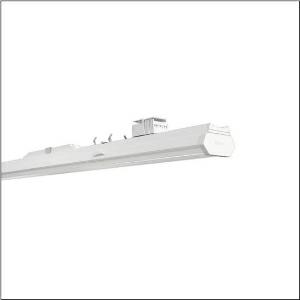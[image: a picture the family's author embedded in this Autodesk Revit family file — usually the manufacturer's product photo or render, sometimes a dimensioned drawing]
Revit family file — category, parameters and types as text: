
# Revit family: licross_r__11_protected_mo_51tp12dn495g3s4_346c
name_source: partatom
category: Lighting Fixtures
units: mm (PartAtom-declared; Revit-internal decimal feet)

## family parameters
Cut with Voids When Loaded = No
Host = Face
Light Source = No
Part Type = Normal
Room Calculation Point = No
Round Connector Dimension = Use Diameter
Shared = No

## types (1)
- --- (1 x LED, 980 lm, 6.8 W, 4000K)
    Apparent Load = 7 VA
    CIE Flux Codes = 73 92 98 99 100
    Color Rendering = 80
    Color Temperature = 4000K
    Default Elevation = 1800 mm
    Description = Licross® 11 Protected MO, luminaire insert, of sheet steel, galvanised, coil coated, white, length: 1.500mm, width: 90mm, height: 101mm, LED rated luminous flux: 9.980lm, light colour: 840, control gear: DALI 2, with plug, 6-pole, with phase selection, for trunking rail, 9 or 11-core, mains connection: 220..240V, AC, 50/60Hz, rated input power: 61W, for trunking rail, 9-/11-core, internal wiring halogen-free, for emergency light function, converter,control gear: single battery element, battery: LiFePO4, 9Ah, primary light control with lens, of plastic, primary optical cover: cover, of PMMA, light emission: direct distribution, primary light characteristic: symmetric, protection rating (complete): IP64, insulation class (complete): insulation class I (protective earthing), certification: CE, UKCA, protection symbol: D if used in an environment with conductive dust loads with corresponding accessories, impact resistance: IK06, permissible ambient temperature for indoor applications: +5..+35°C, standard: EN 60598-2-22, LABS conformity tested according to VDMA 24364:2018-05, reducing of maximum allowable ambient temperature of 5°C with ceiling mounting, corresponds to IFS (International Featured Standards) requirements for safety and quality in the food industry, packaging unit: 1 piece
    Height = 92 mm
    Lamp = 1 x LED
    Lamp Light Flux = 980 lm
    Lamp Power = 6.8 W
    Lamp count = 1
    Length = 1500 mm
    Luminous efficacy = 144 lm/W
    Manufacturer = Siteco
    ModVariant = No
    Model = 51TP12DN495G3S4
    Mounting Place = Ceiling
    Mounting Type = Pendant
    Number of Poles = 1
    OnlyDefault = Yes
    Power Factor = 1
    Product Name = Licross® 11 Protected MO
    Product group = luminaire insert | ceiling pendant
    ProductGroupID = 902
    Protection Class = Protection class I
    Protection Degree = IP 64
    RLX_Detail_Level = 1
    RLX_Emergency_Light_Flux = 0 lm
    RLX_Emergency_Type = 0
    RLX_Emergency_Type_DB = No
    RlxData = <blob elided: 24749 chars, md5=df0dbbae>
    Socket = socket
    Standby Power = 0 W
    System Light Flux = 980 lm
    System Power = 7 W
    Type Comments = : emergency light operation: 3 h
    Type Image = l_1256148.jpg
    URL = http://relux.com
    VarID = @adj_112101
    Voltage = 0 V
    Weight = 0.00 kg
    Width = 88 mm

## geometry (parser evidence)
native form markers: Blend x4, Sweep x11
no freeform markers — native parametric forms only
